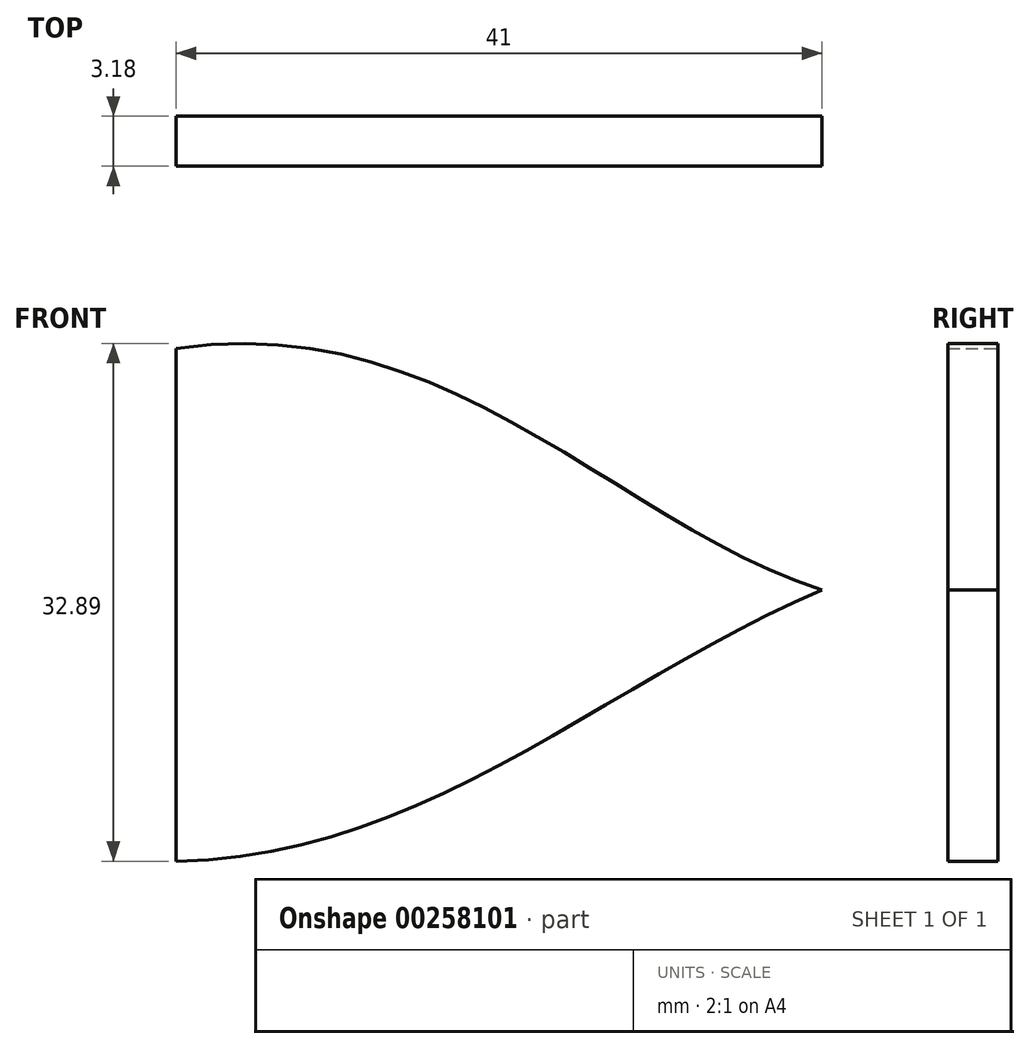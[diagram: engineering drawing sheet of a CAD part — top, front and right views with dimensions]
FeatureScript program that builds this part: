
annotation { "Feature Type Name" : "Feature", "Feature Type Description" : "" }
export const myFeature = defineFeature(function(context is Context, id is Id, definition is map)
    precondition{}
    {
        {
            var Q0;
            Q0=qCreatedBy(makeId("Front.planeOp"),FACE);
            var sketch = newSketch(context, id + "F0", { "sketchPlane" : qUnion([Q0])});
            skLineSegment(sketch, "E0", {"start": v(-20.38, 15.35) * mm, "end": v(-20.38, -17.22) * mm});
            skFitSpline(sketch, "E1", {"points": [v(-20.38, 15.35) * mm, v(20.62, 0) * mm], "startDerivative": vector(52.01, 7.73) * mm, "endDerivative": vector(39.13, -12.65) * mm});
            skFitSpline(sketch, "E2", {"points": [v(-20.38, -17.22) * mm, v(20.62, 0) * mm], "startDerivative": vector(47.8, 0.7) * mm, "endDerivative": vector(41, 17.22) * mm});
            skSolve(sketch);
        }
        {
            var Q0;
            Q0 = qSketchRegion(id + "F0", true);
            extrude(context, id + "F1", {"entities" : qUnion([Q0]), "depth" : 3.17 * mm});
        }
    });
